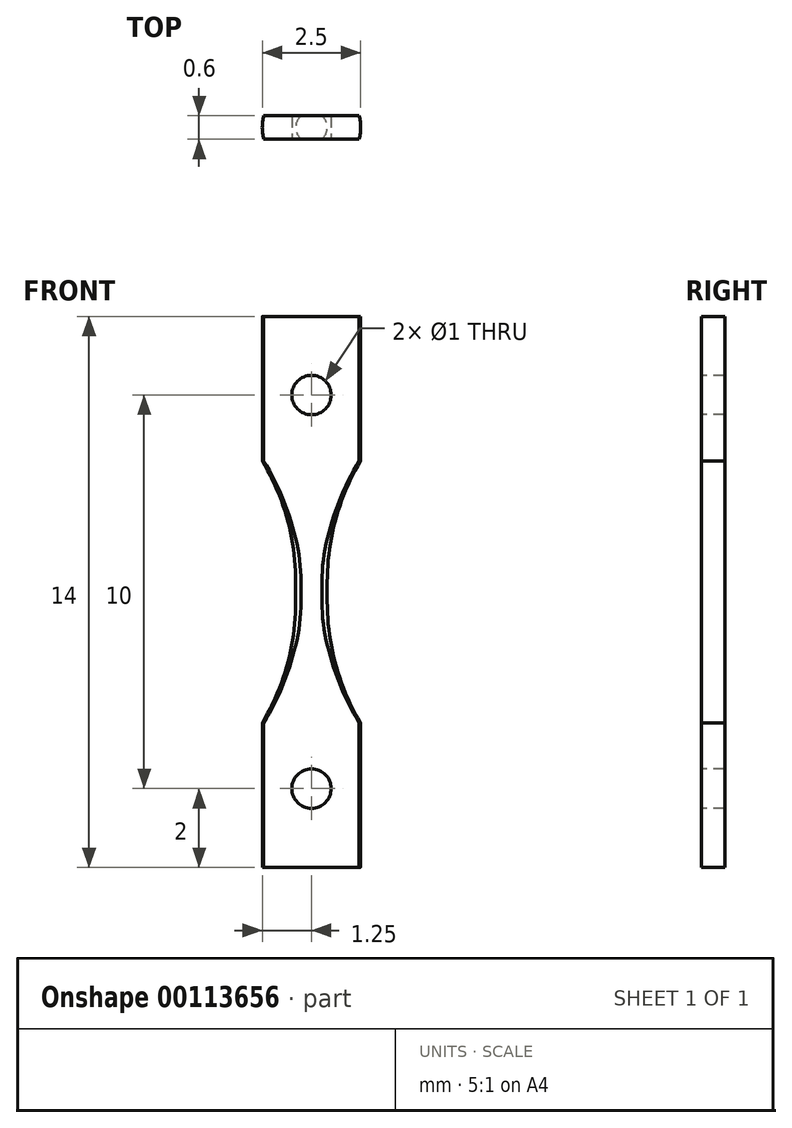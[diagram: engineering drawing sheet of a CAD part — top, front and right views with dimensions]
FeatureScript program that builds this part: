
annotation { "Feature Type Name" : "Feature", "Feature Type Description" : "" }
export const myFeature = defineFeature(function(context is Context, id is Id, definition is map)
    precondition{}
    {
        {
            var Q0;
            Q0=qCreatedBy(makeId("Front.planeOp"),FACE);
            var sketch = newSketch(context, id + "F0", { "sketchPlane" : qUnion([Q0])});
            skLineSegment(sketch, "E0", {"start": v(0, 7) * mm, "end": v(0, 0) * mm});
            skPoint(sketch, "E1", {"position": v(6.4, 0.25) * mm});
            skArc(sketch, "E2", {"start": v(0.4, 0.25) * mm, "mid": v(2.16, 4.5) * mm, "end": v(6.4, 6.25) * mm, "construction": true});
            skLineSegment(sketch, "E3", {"start": v(0, 7) * mm, "end": v(1.25, 7) * mm});
            skLineSegment(sketch, "E4", {"start": v(1.25, 7) * mm, "end": v(1.25, 3.33) * mm});
            skArc(sketch, "E5", {"start": v(0.4, 0.25) * mm, "mid": v(0.62, 1.85) * mm, "end": v(1.25, 3.33) * mm});
            skLineSegment(sketch, "E6", {"start": v(0, 0.25) * mm, "end": v(0.4, 0.25) * mm});
            skLineSegment(sketch, "E7.MirrorCS", {"start": v(0, -7) * mm, "end": v(0, 0) * mm});
            skLineSegment(sketch, "E8.MirrorCS", {"start": v(0, -0.25) * mm, "end": v(0.4, -0.25) * mm});
            skArc(sketch, "E9.MirrorCS", {"start": v(0.4, -0.25) * mm, "mid": v(2.16, -4.5) * mm, "end": v(6.4, -6.25) * mm, "construction": true});
            skLineSegment(sketch, "E10.MirrorCS", {"start": v(1.25, -7) * mm, "end": v(1.25, -3.33) * mm});
            skLineSegment(sketch, "E11.MirrorCS", {"start": v(0, -7) * mm, "end": v(1.25, -7) * mm});
            skArc(sketch, "E12", {"start": v(0.4, -0.25) * mm, "mid": v(0.62, -1.85) * mm, "end": v(1.25, -3.33) * mm});
            skLineSegment(sketch, "E13", {"start": v(0.4, 0.25) * mm, "end": v(0.4, 0.25) * mm});
            skLineSegment(sketch, "E14", {"start": v(0.4, -0.25) * mm, "end": v(0.4, -0.25) * mm});
            skLineSegment(sketch, "E15", {"start": v(0.4, 0.25) * mm, "end": v(0.4, -0.25) * mm});
            skSolve(sketch);
        }
        {
            var Q0;
            {var subQ2=sQuery(id+"F0.wireOp",EDGE,"EKo1FYz1-TvUf-vg46-3QCV-TdD0xKtM2FVf");Q0=makeQuery(id+"F0.imprint","IMPRINT",FACE,{"disambiguationData":[TD([[makeQuery(id+"F0.imprint","IMPRINT",EDGE,{"derivedFrom":subQ2}),1.0]])]});}
            var Q1;
            {var subQ0=sQuery(id+"F0.wireOp",EDGE,"EKo1FYz1-TvUf-vg46-3QCV-TdD0xKtM2FVf");Q1=makeQuery(id+"F0.imprint","IMPRINT",FACE,{"disambiguationData":[TD([[makeQuery(id+"F0.imprint","IMPRINT",EDGE,{"derivedFrom":subQ0}),-1.0]])]});}
            var Q2;
            {var subQ1=sQuery(id+"F0.wireOp",EDGE,"E3");Q2=makeQuery(id+"F0.imprint","IMPRINT",FACE,{"disambiguationData":[TD([[makeQuery(id+"F0.imprint","IMPRINT",EDGE,{"derivedFrom":subQ1}),-1.0]])]});}
            var Q3;
            Q3=sQuery(id+"F0.wireOp",EDGE,"E0");
            revolve(context, id + "F1", {"entities" : qUnion([Q0, Q1, Q2]), "axis" : qUnion([Q3]), "revolveType" : RevolveType.FULL});
        }
        {
            var Q0;
            {var subQ0=sQuery(id+"F0.wireOp",EDGE,"FAY0BoeA-ddRC-77QY-SOEF-yvcMaOBgnlRh");Q0=makeQuery(id+"F0.imprint","IMPRINT",FACE,{"disambiguationData":[TD([[makeQuery(id+"F0.imprint","IMPRINT",EDGE,{"derivedFrom":subQ0}),1.0]])]});}
            var Q1;
            {var subQ0=sQuery(id+"F0.wireOp",EDGE,"FAY0BoeA-ddRC-77QY-SOEF-yvcMaOBgnlRh");Q1=makeQuery(id+"F0.imprint","IMPRINT",FACE,{"disambiguationData":[TD([[makeQuery(id+"F0.imprint","IMPRINT",EDGE,{"derivedFrom":subQ0}),-1.0]])]});}
            var Q2;
            {var subQ4=sQuery(id+"F0.wireOp",EDGE,"E6");Q2=makeQuery(id+"F0.imprint","IMPRINT",FACE,{"disambiguationData":[TD([[makeQuery(id+"F0.imprint","IMPRINT",EDGE,{"derivedFrom":subQ4}),-1.0]])]});}
            var Q3;
            Q3=sQuery(id+"F0.wireOp",EDGE,"E0");
            revolve(context, id + "F2", {"entities" : qUnion([Q0, Q1, Q2]), "axis" : qUnion([Q3]), "revolveType" : RevolveType.FULL});
        }
        {
            var Q0;
            Q0=qCreatedBy(makeId("Front.planeOp"),FACE);
            var sketch = newSketch(context, id + "F3", { "sketchPlane" : qUnion([Q0])});
            skLineSegment(sketch, "E16", {"start": v(1.25, 7.75) * mm, "end": v(0, 7.75) * mm});
            skLineSegment(sketch, "E17", {"start": v(1.25, 7.75) * mm, "end": v(1.25, 0.25) * mm});
            skLineSegment(sketch, "E18", {"start": v(1.25, -0.25) * mm, "end": v(0, -0.25) * mm});
            skLineSegment(sketch, "E19.MirrorCS", {"start": v(-1.25, 7.75) * mm, "end": v(0, 7.75) * mm});
            skLineSegment(sketch, "E20.MirrorCS", {"start": v(-1.25, 7.75) * mm, "end": v(-1.25, 0.25) * mm});
            skLineSegment(sketch, "E21.MirrorCS", {"start": v(-1.25, -0.25) * mm, "end": v(0, -0.25) * mm});
            skLineSegment(sketch, "E22", {"start": v(-1.25, 0.25) * mm, "end": v(-1.25, -0.25) * mm});
            skLineSegment(sketch, "E23", {"start": v(1.25, 0.25) * mm, "end": v(1.25, -0.25) * mm});
            skSolve(sketch);
        }
        {
            var Q0;
            Q0=makeQuery(id+"F3.imprint","IMPRINT",FACE,{"disambiguationData":[TD([[makeQuery(id+"F3.imprint","IMPRINT",EDGE,{"derivedFrom":sQuery(id+"F3.wireOp",EDGE,"E16")}),1.0]])]});
            var Q1;
            Q1=makeQuery(id+"F3.imprint","IMPRINT",FACE,{"disambiguationData":[TD([[makeQuery(id+"F3.imprint","IMPRINT",EDGE,{"derivedFrom":sQuery(id+"F3.wireOp",EDGE,"fd5adca2-b2b1-48c8-ac30-493d49553da9")}),-1.0]])]});
            extrude(context, id + "F4", {"entities" : qUnion([Q0, Q1]), "operationType" : NewBodyOperationType.INTERSECT, "offsetDistance" : 25 * mm, "depth" : 0.6 * mm, "symmetric" : true});
        }
        {
            var Q0;
            Q0=qCreatedBy(makeId("Front.planeOp"),FACE);
            var sketch = newSketch(context, id + "F5", { "sketchPlane" : qUnion([Q0])});
            skPoint(sketch, "E24", {"position": v(0, 5) * mm});
            skCircle(sketch, "E25", {"center": v(0, 5) * mm, "radius": 0.5 * mm});
            skSolve(sketch);
        }
        {
            var Q0;
            Q0=makeQuery(id+"F5.imprint","IMPRINT",FACE,{"disambiguationData":[TD([[makeQuery(id+"F5.imprint","IMPRINT",EDGE,{"derivedFrom":sQuery(id+"F5.wireOp",EDGE,"E25")}),1.0]])]});
            extrude(context, id + "F6", {"entities" : qUnion([Q0]), "operationType" : NewBodyOperationType.REMOVE, "oppositeDirection" : true, "depth" : 25 * mm, "symmetric" : true});
        }
        {
            var Q0;
            Q0=makeQuery(id+"F1.opRevolve","SWEPT_BODY",BODY,{"disambiguationData":[OSD([sQuery(id+"F0.wireOp",EDGE,"OcnPvCSy-cZS5-JDQh-wchw-9l9LrSL49Ts8"),sQuery(id+"F0.wireOp",EDGE,"Dct7jnFl-Wa0s-DOEL-NKnk-l80QN2pxv5ud"),sQuery(id+"F0.wireOp",EDGE,"dMe9K8Vx-obDh-k0uA-Upyp-ExFzSnsmPXVj"),sQuery(id+"F0.wireOp",EDGE,"ASEVp0sq-exOI-wicY-23Um-DL8Uq5OcPyFh"),sQuery(id+"F0.wireOp",EDGE,"b3V7QA5D-BfOZ-9Ogp-569r-IGBEo0v84lE0"),sQuery(id+"F0.wireOp",EDGE,"E0"),sQuery(id+"F0.wireOp",EDGE,"FAY0BoeA-ddRC-77QY-SOEF-yvcMaOBgnlRh")])]});
            var Q1;
            Q1=qCreatedBy(makeId("Top.planeOp"),FACE);
            mirror(context, id + "F7", {"operationType" : NewBodyOperationType.ADD, "entities" : qUnion([Q0]), "mirrorPlane" : qUnion([Q1])});
        }
    });
